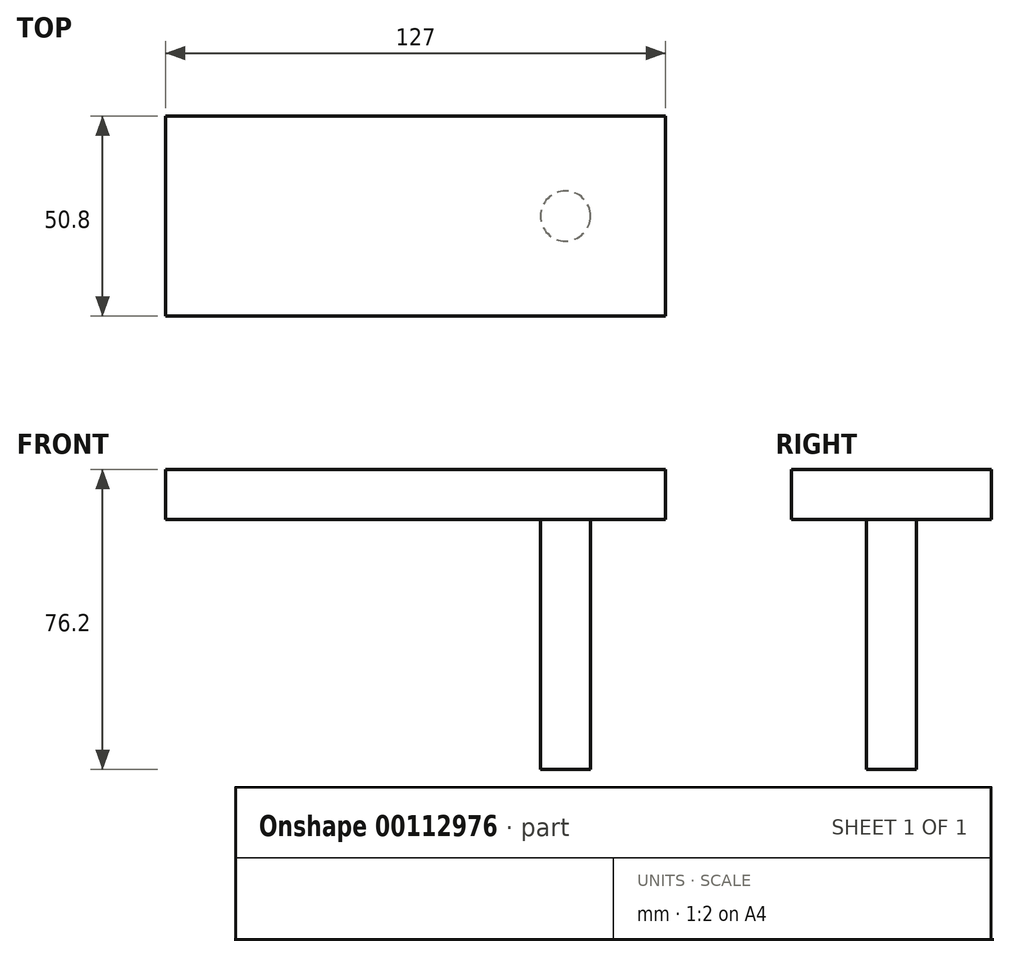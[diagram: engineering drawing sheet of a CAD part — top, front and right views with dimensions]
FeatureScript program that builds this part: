
annotation { "Feature Type Name" : "Feature", "Feature Type Description" : "" }
export const myFeature = defineFeature(function(context is Context, id is Id, definition is map)
    precondition{}
    {
        {
            var Q0;
            Q0=qCreatedBy(makeId("Top.planeOp"),FACE);
            var sketch = newSketch(context, id + "F0", { "sketchPlane" : qUnion([Q0])});
            skCircle(sketch, "E0", {"center": v(0, 0) * mm, "radius": 6.35 * mm});
            skSolve(sketch);
        }
        {
            var Q0;
            Q0=qCreatedBy(makeId("Top.planeOp"),FACE);
            var sketch = newSketch(context, id + "F1", { "sketchPlane" : qUnion([Q0])});
            skLineSegment(sketch, "E1.bottom", {"start": v(25.4, 25.4) * mm, "end": v(-101.6, 25.4) * mm});
            skLineSegment(sketch, "E1.top", {"start": v(25.4, -25.4) * mm, "end": v(-101.6, -25.4) * mm});
            skLineSegment(sketch, "E1.left", {"start": v(25.4, 25.4) * mm, "end": v(25.4, -25.4) * mm});
            skLineSegment(sketch, "E1.right", {"start": v(-101.6, 25.4) * mm, "end": v(-101.6, -25.4) * mm});
            skSolve(sketch);
        }
        {
            var Q0;
            Q0=makeQuery(id+"F0.imprint","IMPRINT",FACE,{"disambiguationData":[TD([[makeQuery(id+"F0.imprint","IMPRINT",EDGE,{"derivedFrom":sQuery(id+"F0.wireOp",EDGE,"E0")}),1.0]])]});
            extrude(context, id + "F2", {"entities" : qUnion([Q0]), "oppositeDirection" : true, "depth" : 63.5 * mm});
        }
        {
            var Q0;
            Q0=makeQuery(id+"F1.imprint","IMPRINT",FACE,{"disambiguationData":[TD([[makeQuery(id+"F1.imprint","IMPRINT",EDGE,{"derivedFrom":sQuery(id+"F1.wireOp",EDGE,"E1.bottom")}),1.0]])]});
            extrude(context, id + "F3", {"entities" : qUnion([Q0]), "operationType" : NewBodyOperationType.ADD, "depth" : 12.7 * mm});
        }
    });
